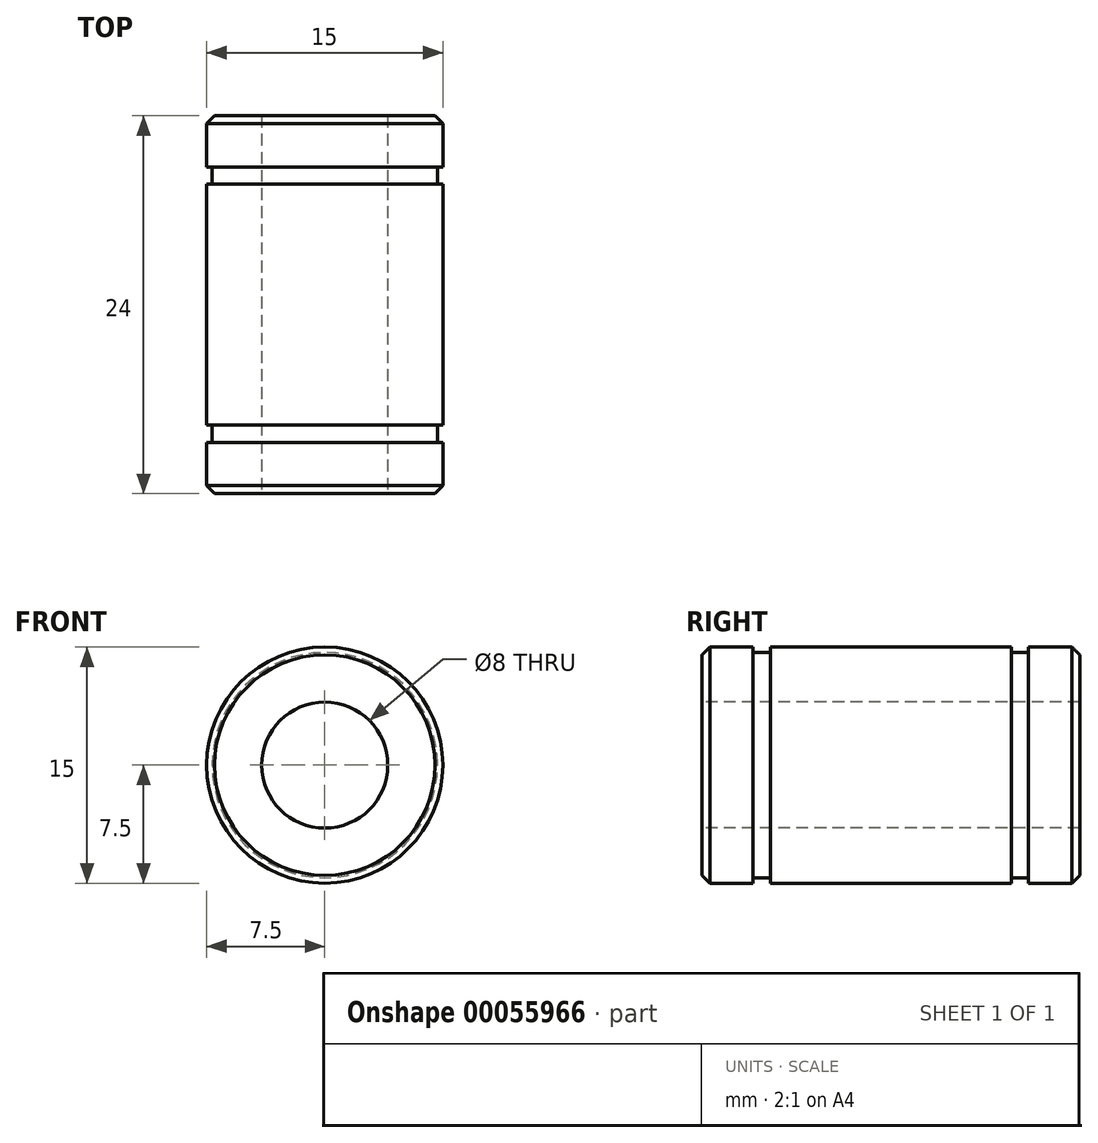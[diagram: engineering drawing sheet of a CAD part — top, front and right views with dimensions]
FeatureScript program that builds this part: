
annotation { "Feature Type Name" : "Feature", "Feature Type Description" : "" }
export const myFeature = defineFeature(function(context is Context, id is Id, definition is map)
    precondition{}
    {
        {
            var Q0;
            Q0=qCreatedBy(makeId("Front.planeOp"),FACE);
            var sketch = newSketch(context, id + "F0", { "sketchPlane" : qUnion([Q0])});
            skCircle(sketch, "E0", {"center": v(0, 0) * mm, "radius": 4 * mm});
            skSolve(sketch);
        }
        {
            var Q0;
            Q0=qCreatedBy(makeId("Right.planeOp"),FACE);
            var sketch = newSketch(context, id + "F1", { "sketchPlane" : qUnion([Q0])});
            skLineSegment(sketch, "E1.0", {"start": v(0, -4) * mm, "end": v(0, 4) * mm});
            skLineSegment(sketch, "E2.bottom", {"start": v(0, 4) * mm, "end": v(24, 4) * mm});
            skLineSegment(sketch, "E2.top", {"start": v(0, 7.5) * mm, "end": v(24, 7.5) * mm});
            skLineSegment(sketch, "E2.left", {"start": v(0, 4) * mm, "end": v(0, 7.5) * mm});
            skLineSegment(sketch, "E2.right", {"start": v(24, 4) * mm, "end": v(24, 7.5) * mm});
            skLineSegment(sketch, "E3", {"start": v(12, 7.5) * mm, "end": v(20.75, 7.5) * mm});
            skLineSegment(sketch, "E4", {"start": v(12, 7.5) * mm, "end": v(3.25, 7.5) * mm});
            skLineSegment(sketch, "E5.bottom", {"start": v(3.25, 7.5) * mm, "end": v(4.35, 7.5) * mm});
            skLineSegment(sketch, "E5.top", {"start": v(3.25, 7.15) * mm, "end": v(4.35, 7.15) * mm});
            skLineSegment(sketch, "E5.left", {"start": v(3.25, 7.5) * mm, "end": v(3.25, 7.15) * mm});
            skLineSegment(sketch, "E5.right", {"start": v(4.35, 7.5) * mm, "end": v(4.35, 7.15) * mm});
            skLineSegment(sketch, "E6.bottom", {"start": v(20.75, 7.5) * mm, "end": v(19.65, 7.5) * mm});
            skLineSegment(sketch, "E6.top", {"start": v(20.75, 7.15) * mm, "end": v(19.65, 7.15) * mm});
            skLineSegment(sketch, "E6.left", {"start": v(20.75, 7.5) * mm, "end": v(20.75, 7.15) * mm});
            skLineSegment(sketch, "E6.right", {"start": v(19.65, 7.5) * mm, "end": v(19.65, 7.15) * mm});
            skLineSegment(sketch, "E7.bottom", {"start": v(0, 7.5) * mm, "end": v(0.5, 7.5) * mm});
            skLineSegment(sketch, "E7.left", {"start": v(0, 7.5) * mm, "end": v(0, 7) * mm});
            skLineSegment(sketch, "E8.bottom", {"start": v(24, 7.5) * mm, "end": v(23.5, 7.5) * mm});
            skLineSegment(sketch, "E8.left", {"start": v(24, 7.5) * mm, "end": v(24, 7) * mm});
            skLineSegment(sketch, "E9", {"start": v(0, 7) * mm, "end": v(0.5, 7.5) * mm});
            skLineSegment(sketch, "E10", {"start": v(23.5, 7.5) * mm, "end": v(24, 7) * mm});
            skSolve(sketch);
        }
        {
            var Q0;
            Q0=makeQuery(id+"F1.imprint","IMPRINT",FACE,{"disambiguationData":[TD([[makeQuery(id+"F1.imprint","IMPRINT",EDGE,{"derivedFrom":sQuery(id+"F1.wireOp",EDGE,"E2.bottom")}),1.0]])]});
            var Q1;
            Q1=sQuery(id+"F0.wireOp",EDGE,"E0");
            sweep(context, id + "F2", {"profiles" : qUnion([Q0]), "path" : qUnion([Q1])});
        }
    });
